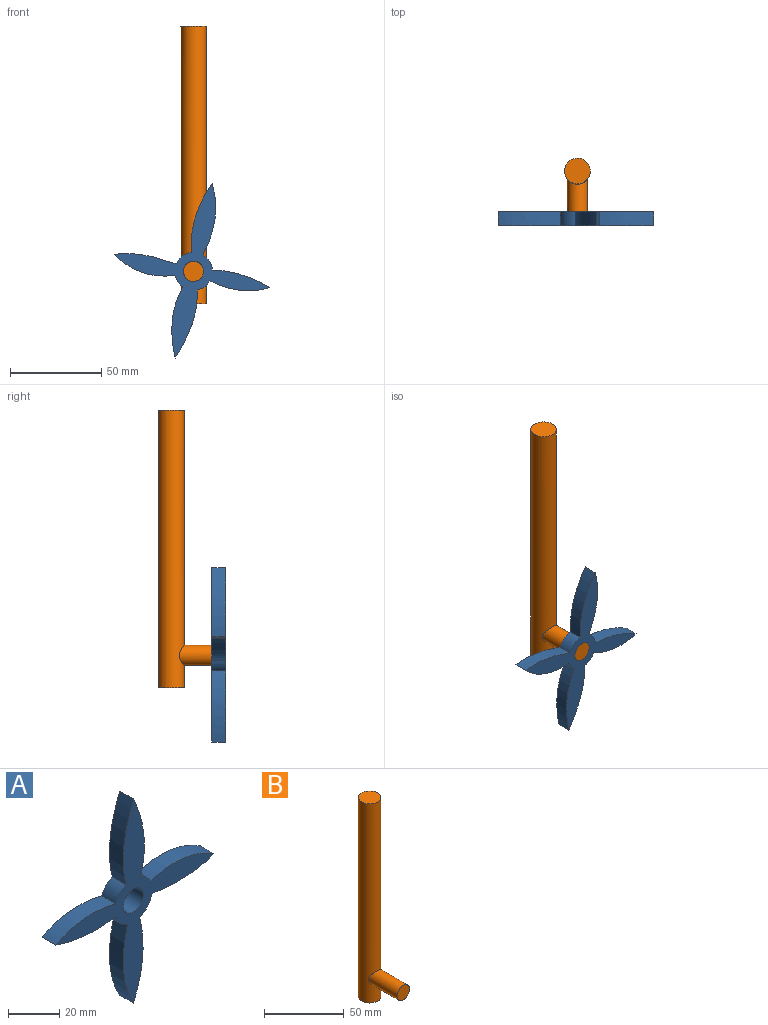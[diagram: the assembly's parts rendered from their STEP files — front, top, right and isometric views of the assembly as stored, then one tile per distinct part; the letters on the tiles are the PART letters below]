
ASSEMBLY  parts=2 mates=1
PART A: 15 faces, bbox 87.4x7.6x97.7 mm
  f0: extruded ~35.06x7.62mm, area 279.5mm2, adj f1,f11,f13,f14
  f1: cylinder r=10.39mm len=7.62mm, axis (0,1,0), area 59.2mm2, adj f0,f2,f13,f14
  f2: extruded ~38.98x7.62mm, area 305.7mm2, adj f1,f3,f13,f14
  f3: extruded ~39x7.62mm, area 303.9mm2, adj f2,f4,f13,f14
  f4: cylinder r=10.39mm len=7.62mm, axis (0,1,0), area 67.2mm2, adj f3,f5,f13,f14
  f5: extruded ~32.98x7.62mm, area 259mm2, adj f4,f6,f13,f14
  f6: extruded ~32.86x7.62mm, area 254.3mm2, adj f5,f7,f13,f14
  f7: cylinder r=10.39mm len=7.62mm, axis (0,1,0), area 76.9mm2, adj f6,f8,f13,f14
  f8: extruded ~39.26x7.62mm, area 308.1mm2, adj f7,f9,f13,f14
  f9: extruded ~39.32x7.62mm, area 306.7mm2, adj f8,f10,f13,f14
  f10: cylinder r=10.39mm len=7.84mm, axis (0,1,0), area 82.6mm2, adj f9,f11,f13,f14
  f11: extruded ~34.31x7.62mm, area 264.9mm2, adj f0,f10,f13,f14
  f12: cylinder r=5.52mm len=11.04mm, axis (0,1,0), area 264.3mm2, adj f13,f14
  f13: plane 97.69x87.36mm, normal (0,-1,0), area 1377.3mm2, adj f0,f1,f2,f3,f4,f5,f6,f7
  f14: plane 97.69x87.36mm, normal (0,1,0), area 1377.3mm2, adj f0,f1,f2,f3,f4,f5,f6,f7
PART B: 5 faces, bbox 14.1x36.7x152.4 mm
  f0: cylinder r=7.03mm len=152.4mm, axis (0,0,-1), area 6623.7mm2, adj f1,f2,f3
  f1: plane 14.06x14.06mm, normal (0,0,1), area 155.2mm2, adj f0
  f2: plane 14.06x14.06mm, normal (0,0,-1), area 155.2mm2, adj f0
  f3: cylinder r=5.52mm len=25.37mm, axis (0,1,0), area 830.8mm2, adj f0,f4
  f4: plane 11.04x11.04mm, normal (0,-1,0), area 95.7mm2, adj f3
PLACE A rot(axis=(0,-1,0),168deg) t=(-33.72,34,14.12)mm
PLACE B t=(-37.43,26.38,-21.22)mm fixed
MATE revolute A.f1 <-> B.f3  axis (0,-1,0) through (-37.43,-3.33,-3.36)mm
